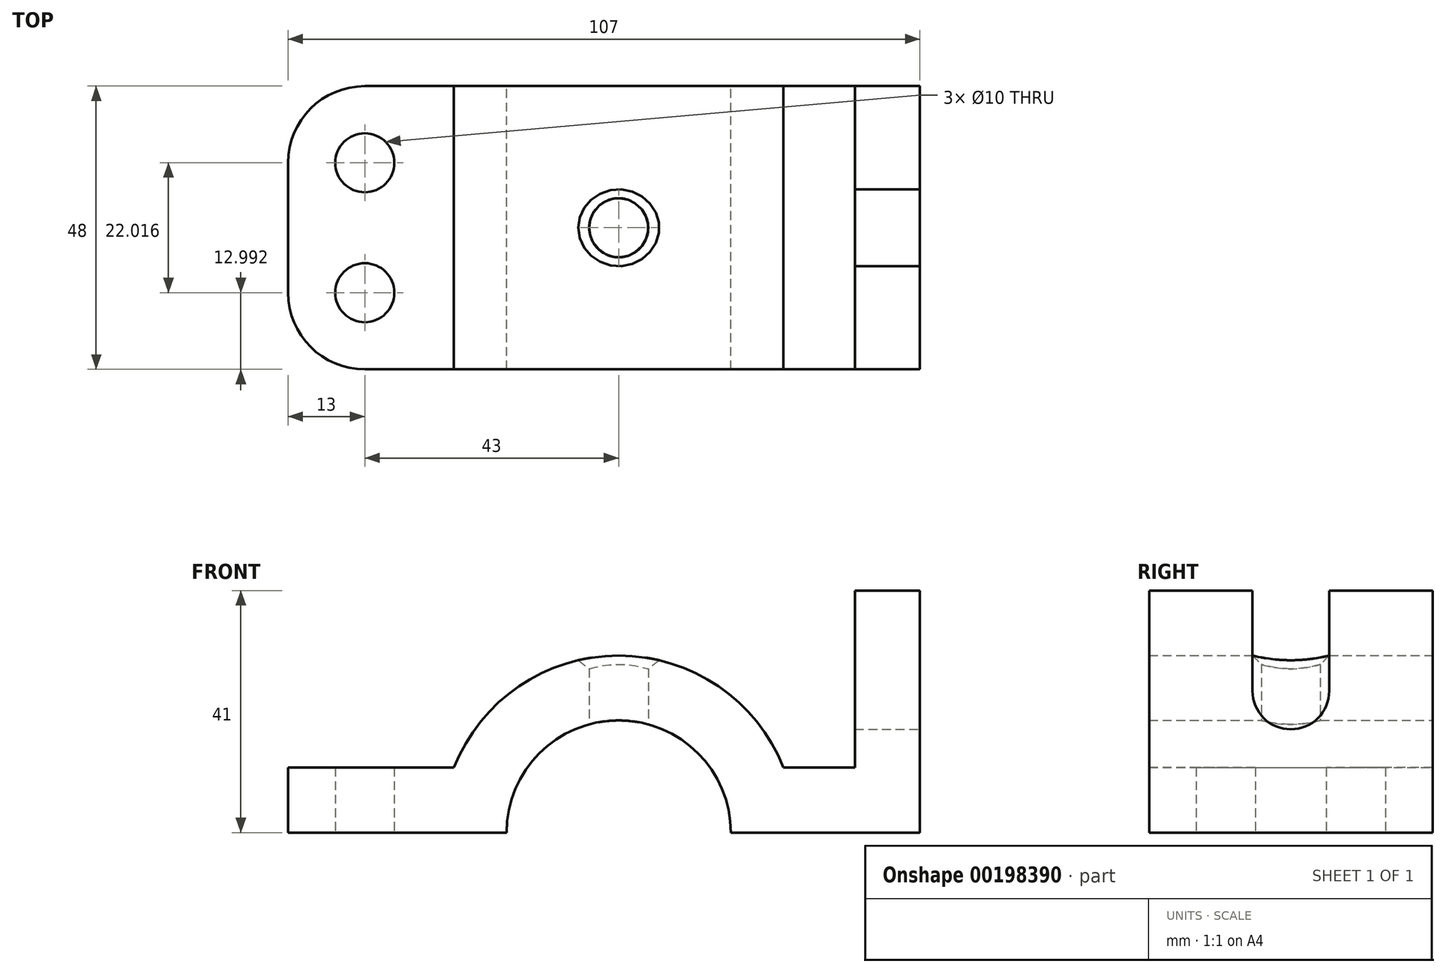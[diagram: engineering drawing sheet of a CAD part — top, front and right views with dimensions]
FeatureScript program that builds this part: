
annotation { "Feature Type Name" : "Feature", "Feature Type Description" : "" }
export const myFeature = defineFeature(function(context is Context, id is Id, definition is map)
    precondition{}
    {
        {
            var Q0;
            Q0=qCreatedBy(makeId("Front.planeOp"),FACE);
            var sketch = newSketch(context, id + "F0", { "sketchPlane" : qUnion([Q0])});
            skArc(sketch, "E0", {"start": v(19, 0) * mm, "mid": v(0, 19) * mm, "end": v(-19, 0) * mm});
            skLineSegment(sketch, "E1", {"start": v(-19, 0) * mm, "end": v(-56, 0) * mm});
            skLineSegment(sketch, "E2", {"start": v(-56, 0) * mm, "end": v(-56, 11) * mm});
            skLineSegment(sketch, "E3", {"start": v(19, 0) * mm, "end": v(51, 0) * mm});
            skLineSegment(sketch, "E4", {"start": v(51, 0) * mm, "end": v(51, 41) * mm});
            skLineSegment(sketch, "E5", {"start": v(51, 41) * mm, "end": v(40, 41) * mm});
            skArc(sketch, "E6.0", {"start": v(27.91, 11) * mm, "mid": v(0, 30) * mm, "end": v(-27.91, 11) * mm});
            skLineSegment(sketch, "E7", {"start": v(-56, 11) * mm, "end": v(-27.91, 11) * mm});
            skLineSegment(sketch, "E8.0", {"start": v(27.91, 11) * mm, "end": v(51, 11) * mm});
            skLineSegment(sketch, "E9", {"start": v(40, 41) * mm, "end": v(40, 11) * mm});
            skSolve(sketch);
        }
        {
            var Q0;
            {var subQ0=sQuery(id+"F0.wireOp",EDGE,"E5");Q0=makeQuery(id+"F0.imprint","IMPRINT",FACE,{"disambiguationData":[TD([[makeQuery(id+"F0.imprint","IMPRINT",EDGE,{"derivedFrom":subQ0}),1.0]])]});}
            var Q1;
            Q1=makeQuery(id+"F0.imprint","IMPRINT",FACE,{"disambiguationData":[TD([[makeQuery(id+"F0.imprint","IMPRINT",EDGE,{"derivedFrom":sQuery(id+"F0.wireOp",EDGE,"E0")}),-1.0]])]});
            extrude(context, id + "F1", {"entities" : qUnion([Q0, Q1]), "endBound" : BoundingType.SYMMETRIC, "depth" : 48 * mm});
        }
        {
            var Q0;
            Q0=qCreatedBy(makeId("Top.planeOp"),FACE);
            var sketch = newSketch(context, id + "F2", { "sketchPlane" : qUnion([Q0])});
            skLineSegment(sketch, "E10", {"start": v(-43, 24) * mm, "end": v(-59.96, 24) * mm});
            skCircle(sketch, "E11", {"center": v(-43, 11) * mm, "radius": 5 * mm});
            skArc(sketch, "E12", {"start": v(-43, 24) * mm, "mid": v(-52.2, 20.2) * mm, "end": v(-56, 11) * mm});
            skCircle(sketch, "E13.MirrorC", {"center": v(-43, -11) * mm, "radius": 5 * mm});
            skArc(sketch, "E14.MirrorCS", {"start": v(-43, -24) * mm, "mid": v(-52.2, -20.2) * mm, "end": v(-56, -11) * mm});
            skCircle(sketch, "E15", {"center": v(0, 0) * mm, "radius": 5 * mm});
            skSolve(sketch);
        }
        {
            var Q0;
            Q0 = qSketchRegion(id + "F2", true);
            extrude(context, id + "F3", {"entities" : qUnion([Q0]), "operationType" : NewBodyOperationType.REMOVE, "endBound" : BoundingType.THROUGH_ALL, "depth" : 25 * mm});
        }
        {
            var Q0;
            Q0=makeQuery(id+"F3.boolean.opBoolean","INTERSECT",EDGE,{"derivedFrom":[makeQuery(id+"F1.opExtrude","SWEPT_FACE",FACE,{"disambiguationData":[OSD([sQuery(id+"F0.wireOp",EDGE,"E6.0")])]}),makeQuery(id+"F3.opExtrude","SWEPT_FACE",FACE,{"disambiguationData":[OSD([sQuery(id+"F2.wireOp",EDGE,"E15")])]})]});
            chamfer(context, id + "F4", {"entities" : qUnion([Q0]), "width" : 1.5 * mm, "tangentPropagation" : true});
        }
        {
            var Q0;
            Q0=makeQuery(id+"F1.opExtrude","CAP_EDGE",EDGE,{"disambiguationData":[OSD([sQuery(id+"F0.wireOp",EDGE,"E2")])],"isStart":false});
            fillet(context, id + "F5", {"entities" : qUnion([Q0]), "radius" : 13 * mm, "tangentPropagation" : true, "allowEdgeOverflow" : false});
        }
        {
            var Q0;
            Q0=makeQuery(id+"F1.opExtrude","CAP_EDGE",EDGE,{"disambiguationData":[OSD([sQuery(id+"F0.wireOp",EDGE,"E2")])],"isStart":true});
            fillet(context, id + "F6", {"entities" : qUnion([Q0]), "radius" : 13 * mm, "tangentPropagation" : true, "allowEdgeOverflow" : false});
        }
        {
            var Q0;
            Q0=makeQuery(id+"F1.opExtrude","SWEPT_FACE",FACE,{"disambiguationData":[OSD([sQuery(id+"F0.wireOp",EDGE,"E4")])]});
            var sketch = newSketch(context, id + "F7", { "sketchPlane" : qUnion([Q0])});
            skLineSegment(sketch, "E16", {"start": v(0, 41) * mm, "end": v(0, 0) * mm});
            skLineSegment(sketch, "E17.0", {"start": v(6.5, 41) * mm, "end": v(6.5, 0) * mm});
            skLineSegment(sketch, "E18.0", {"start": v(-6.5, 41) * mm, "end": v(-6.5, 0) * mm});
            skArc(sketch, "E19", {"start": v(-6.5, 24) * mm, "mid": v(0, 17.5) * mm, "end": v(6.5, 24) * mm});
            skLineSegment(sketch, "E20", {"start": v(-6.5, 41) * mm, "end": v(6.5, 41) * mm});
            skLineSegment(sketch, "E21", {"start": v(-6.5, 24) * mm, "end": v(6.5, 24) * mm});
            skSolve(sketch);
        }
        {
            var Q0;
            {var subQ0=sQuery(id+"F7.wireOp",EDGE,"E21");var subQ1=sQuery(id+"F7.wireOp",EDGE,"E16");var subQ2=makeQuery(id+"F7.imprint","INTERSECT",VERTEX,{"derivedFrom":[subQ1,subQ0]});Q0=makeQuery(id+"F7.imprint","IMPRINT",FACE,{"disambiguationData":[TD([[makeQuery(id+"F7.imprint","IMPRINT",EDGE,{"disambiguationData":[TD([[subQ2,-1.0]])],"derivedFrom":subQ1}),1.0]])]});}
            var Q1;
            {var subQ0=sQuery(id+"F7.wireOp",EDGE,"E21");var subQ1=sQuery(id+"F7.wireOp",EDGE,"E16");var subQ2=makeQuery(id+"F7.imprint","INTERSECT",VERTEX,{"derivedFrom":[subQ1,subQ0]});Q1=makeQuery(id+"F7.imprint","IMPRINT",FACE,{"disambiguationData":[TD([[makeQuery(id+"F7.imprint","IMPRINT",EDGE,{"disambiguationData":[TD([[subQ2,-1.0]])],"derivedFrom":subQ1}),-1.0]])]});}
            var Q2;
            {var subQ0=sQuery(id+"F7.wireOp",EDGE,"E20");var subQ1=sQuery(id+"F7.wireOp",EDGE,"E16");var subQ2=makeQuery(id+"F7.imprint","INTERSECT",VERTEX,{"derivedFrom":[subQ1,subQ0]});Q2=makeQuery(id+"F7.imprint","IMPRINT",FACE,{"disambiguationData":[TD([[makeQuery(id+"F7.imprint","IMPRINT",EDGE,{"disambiguationData":[TD([[subQ2,-1.0]])],"derivedFrom":subQ1}),-1.0]])]});}
            var Q3;
            {var subQ0=sQuery(id+"F7.wireOp",EDGE,"E20");var subQ1=sQuery(id+"F7.wireOp",EDGE,"E16");var subQ2=makeQuery(id+"F7.imprint","INTERSECT",VERTEX,{"derivedFrom":[subQ1,subQ0]});Q3=makeQuery(id+"F7.imprint","IMPRINT",FACE,{"disambiguationData":[TD([[makeQuery(id+"F7.imprint","IMPRINT",EDGE,{"disambiguationData":[TD([[subQ2,-1.0]])],"derivedFrom":subQ1}),1.0]])]});}
            extrude(context, id + "F8", {"entities" : qUnion([Q0, Q1, Q2, Q3]), "operationType" : NewBodyOperationType.REMOVE, "oppositeDirection" : true, "depth" : 25 * mm});
        }
    });
